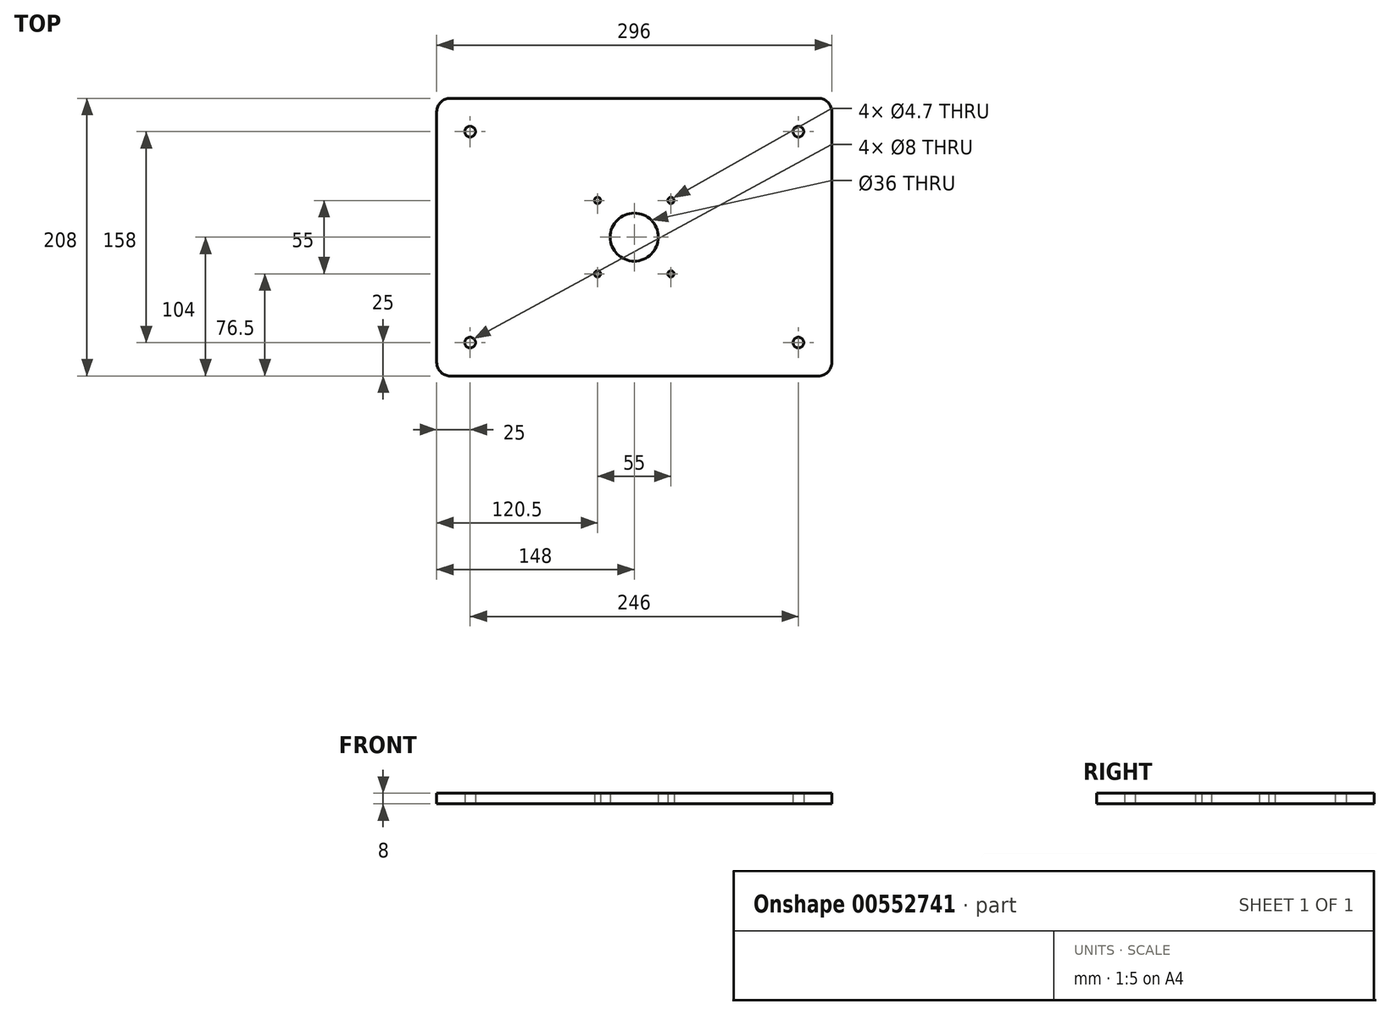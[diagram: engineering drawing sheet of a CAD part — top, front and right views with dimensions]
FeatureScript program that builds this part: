
annotation { "Feature Type Name" : "Feature", "Feature Type Description" : "" }
export const myFeature = defineFeature(function(context is Context, id is Id, definition is map)
    precondition{}
    {
        {
            var Q0;
            Q0=qCreatedBy(makeId("Top.planeOp"),FACE);
            var sketch = newSketch(context, id + "F0", { "sketchPlane" : qUnion([Q0])});
            skLineSegment(sketch, "E0.bottom", {"start": v(-148, 104) * mm, "end": v(148, 104) * mm});
            skLineSegment(sketch, "E0.top", {"start": v(-148, -104) * mm, "end": v(148, -104) * mm});
            skLineSegment(sketch, "E0.left", {"start": v(-148, 104) * mm, "end": v(-148, -104) * mm});
            skLineSegment(sketch, "E0.right", {"start": v(148, 104) * mm, "end": v(148, -104) * mm});
            skPoint(sketch, "E0.middle", {"position": v(0, 0) * mm});
            skCircle(sketch, "E1", {"center": v(0, 0) * mm, "radius": 18 * mm});
            skLineSegment(sketch, "E2.bottom", {"start": v(-27.5, 27.5) * mm, "end": v(27.5, 27.5) * mm, "construction": true});
            skLineSegment(sketch, "E2.top", {"start": v(-27.5, -27.5) * mm, "end": v(27.5, -27.5) * mm, "construction": true});
            skLineSegment(sketch, "E2.left", {"start": v(-27.5, 27.5) * mm, "end": v(-27.5, -27.5) * mm, "construction": true});
            skLineSegment(sketch, "E2.right", {"start": v(27.5, 27.5) * mm, "end": v(27.5, -27.5) * mm, "construction": true});
            skCircle(sketch, "E3", {"center": v(-27.5, 27.5) * mm, "radius": 2.35 * mm});
            skCircle(sketch, "E4", {"center": v(27.5, 27.5) * mm, "radius": 2.35 * mm});
            skCircle(sketch, "E5", {"center": v(27.5, -27.5) * mm, "radius": 2.35 * mm});
            skCircle(sketch, "E6", {"center": v(-27.5, -27.5) * mm, "radius": 2.35 * mm});
            skLineSegment(sketch, "E7.bottom", {"start": v(-123, 79) * mm, "end": v(123, 79) * mm, "construction": true});
            skLineSegment(sketch, "E7.top", {"start": v(-123, -79) * mm, "end": v(123, -79) * mm, "construction": true});
            skLineSegment(sketch, "E7.left", {"start": v(-123, 79) * mm, "end": v(-123, -79) * mm, "construction": true});
            skLineSegment(sketch, "E7.right", {"start": v(123, 79) * mm, "end": v(123, -79) * mm, "construction": true});
            skCircle(sketch, "E8", {"center": v(-123, 79) * mm, "radius": 4 * mm});
            skCircle(sketch, "E9", {"center": v(123, 79) * mm, "radius": 4 * mm});
            skCircle(sketch, "E10", {"center": v(123, -79) * mm, "radius": 4 * mm});
            skCircle(sketch, "E11", {"center": v(-123, -79) * mm, "radius": 4 * mm});
            skSolve(sketch);
        }
        {
            var Q0;
            Q0=makeQuery(id+"F0.imprint","IMPRINT",FACE,{"disambiguationData":[TD([[makeQuery(id+"F0.imprint","IMPRINT",EDGE,{"derivedFrom":sQuery(id+"F0.wireOp",EDGE,"E0.bottom")}),-1.0]])]});
            extrude(context, id + "F1", {"entities" : qUnion([Q0]), "depth" : 8 * mm, "offsetDistance" : 25 * mm});
        }
        {
            var Q0;
            Q0=makeQuery(id+"F1.opExtrude","SWEPT_EDGE",EDGE,{"disambiguationData":[OSD([sQuery(id+"F0.wireOp",EDGE,"E0.bottom"),sQuery(id+"F0.wireOp",EDGE,"E0.left")])]});
            var Q1;
            Q1=makeQuery(id+"F1.opExtrude","SWEPT_EDGE",EDGE,{"disambiguationData":[OSD([sQuery(id+"F0.wireOp",EDGE,"E0.top"),sQuery(id+"F0.wireOp",EDGE,"E0.left")])]});
            var Q2;
            Q2=makeQuery(id+"F1.opExtrude","SWEPT_EDGE",EDGE,{"disambiguationData":[OSD([sQuery(id+"F0.wireOp",EDGE,"E0.top"),sQuery(id+"F0.wireOp",EDGE,"E0.right")])]});
            var Q3;
            Q3=makeQuery(id+"F1.opExtrude","SWEPT_EDGE",EDGE,{"disambiguationData":[OSD([sQuery(id+"F0.wireOp",EDGE,"E0.bottom"),sQuery(id+"F0.wireOp",EDGE,"E0.right")])]});
            fillet(context, id + "F2", {"entities" : qUnion([Q0, Q1, Q2, Q3]), "radius" : 10 * mm, "allowEdgeOverflow" : false});
        }
    });
